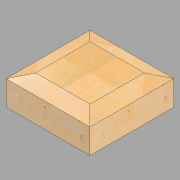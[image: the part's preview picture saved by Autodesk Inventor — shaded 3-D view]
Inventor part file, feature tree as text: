
AUTODESK INVENTOR PART (.ipt)
format: ipt  version: 2022.2 (Build 262287010, 287A)  size: 137,728 bytes
history: native  units: in
note: dims shown in document units (in); Inventor stores cm internally (conversion verified against a paired STEP export)
features: sketch x3, extrude x1, sweep x1
ambient origin geometry x8: Origin, YZ Plane, XZ Plane, XY Plane, X Axis, Y Axis, Z Axis, Center Point
bodies: Solid1 (feature_tree)
feature tree (5):
  extrude  "Extrusion1"  Depth=34.0in
  sweep  "Sweep1"
  sketch  "Sketch1"  dims[d0=34.0in d1=34.0in]
  sketch  "Sketch2"  dims[d2=12.0in d3=0.0in d4=6.0in d5=2.0in d6=0.0in d7=0.0in]
  sketch  "3D Sketch1"
